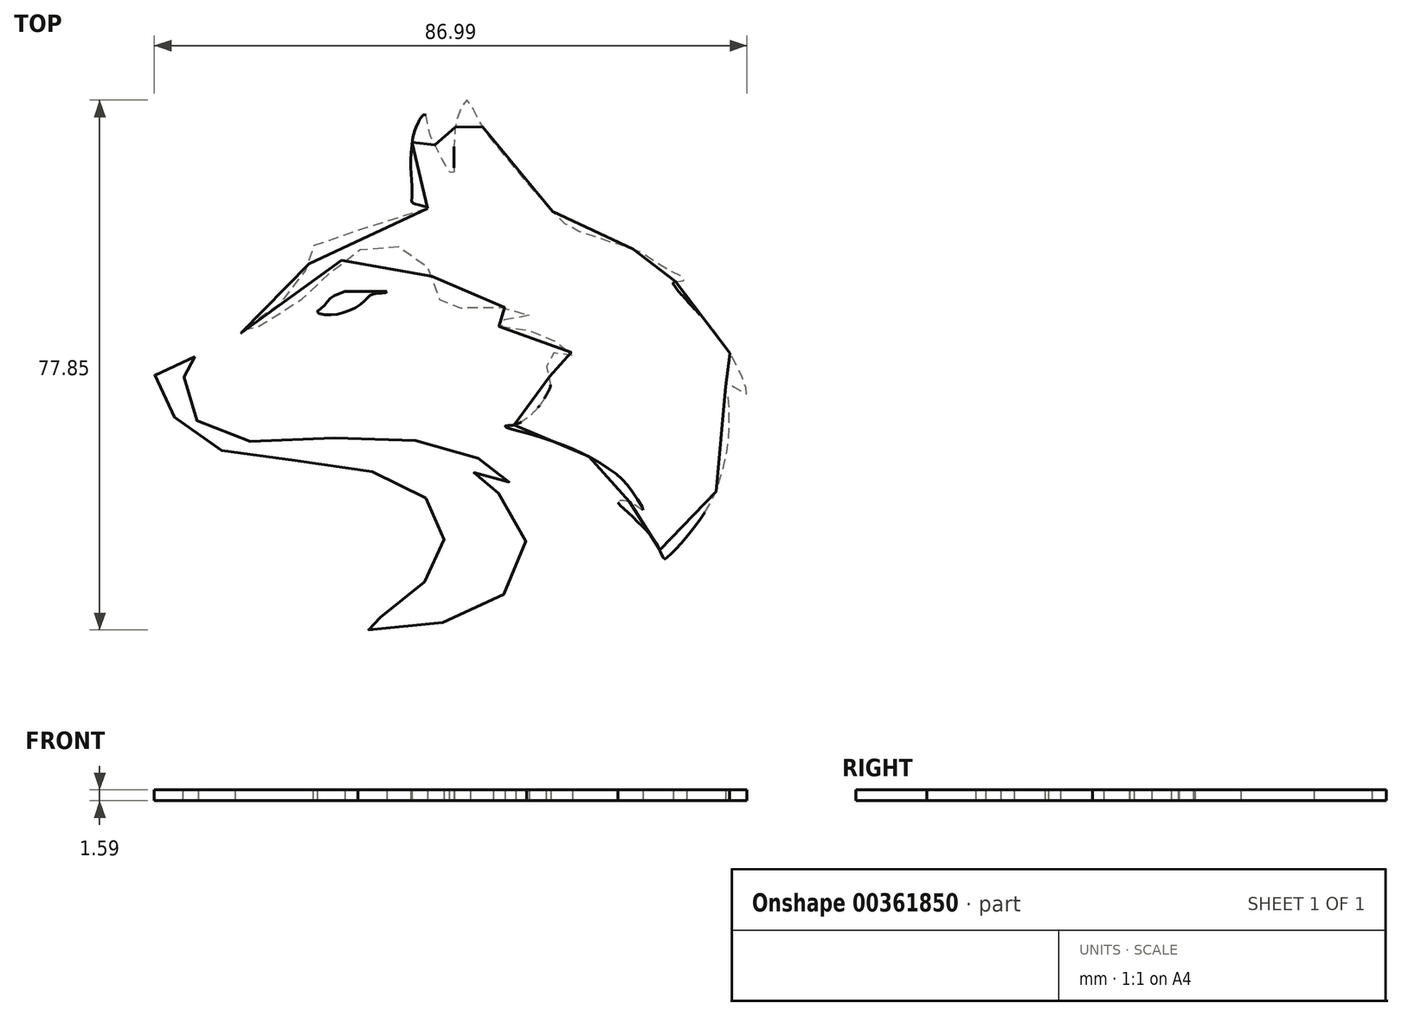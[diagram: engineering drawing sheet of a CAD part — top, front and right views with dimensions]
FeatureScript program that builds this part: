
annotation { "Feature Type Name" : "Feature", "Feature Type Description" : "" }
export const myFeature = defineFeature(function(context is Context, id is Id, definition is map)
    precondition{}
    {
        {
            var Q0;
            Q0=qCreatedBy(makeId("Top.planeOp"),FACE);
            var sketch = newSketch(context, id + "F0", { "sketchPlane" : qUnion([Q0])});
            skLineSegment(sketch, "E0", {"start": v(-16.32, 7.14) * mm, "end": v(-22.48, 7.14) * mm});
            skFitSpline(sketch, "E1", {"points": [v(-22.48, 7.14) * mm, v(-24.21, 6.43) * mm, v(-25.02, 5.67) * mm, v(-25.89, 4.75) * mm, v(-26.55, 4.09) * mm, v(-25.23, 3.68) * mm, v(-23.1, 3.94) * mm, v(-20.85, 4.8) * mm, v(-19.48, 5.87) * mm, v(-18.87, 6.48) * mm, v(-18.18, 6.79) * mm, v(-17.18, 6.91) * mm, v(-16.62, 6.93) * mm, v(-16.32, 7.14) * mm], "startDerivative": vector(-19.93, -6.66) * mm, "endDerivative": vector(6.3, 6.23) * mm});
            skFitSpline(sketch, "E2", {"points": [v(-44.5, -2.46) * mm, v(-47.41, -2.83) * mm, v(-49.23, -3.92) * mm, v(-50.43, -5.36) * mm, v(-49.87, -7.6) * mm, v(-48.8, -9.55) * mm, v(-46.81, -12.25) * mm, v(-44.76, -14.33) * mm, v(-40.01, -16.38) * mm, v(-33.9, -17.35) * mm, v(-27.74, -17.9) * mm, v(-20.44, -18.9) * mm, v(-15.66, -20.2) * mm, v(-11.9, -22.07) * mm, v(-9.77, -24.2) * mm, v(-8.51, -26.32) * mm, v(-7.97, -28.58) * mm, v(-8.15, -30.96) * mm, v(-9.37, -33.55) * mm, v(-10.56, -35.31) * mm, v(-13.6, -38.29) * mm, v(-16.28, -40.2) * mm, v(-18.26, -41.32) * mm, v(-19.45, -41.9) * mm, v(-20.56, -42.5) * mm, v(-19.4, -42.58) * mm, v(-13.55, -42.18) * mm, v(-7.21, -41.32) * mm, v(-1.82, -39.37) * mm, v(1.5, -36.71) * mm, v(3.94, -32.76) * mm, v(4.08, -29.52) * mm, v(2.86, -25.92) * mm, v(0.7, -23.11) * mm, v(-1.31, -21.39) * mm, v(-3.62, -19.95) * mm, v(-4.07, -19.8) * mm, v(-3.92, -19.66) * mm, v(-3.03, -19.36) * mm, v(-1.44, -19.53) * mm, v(0.03, -20.09) * mm, v(1.43, -20.74) * mm, v(2.54, -21.3) * mm, v(2.56, -21.05) * mm, v(-1.4, -18.21) * mm, v(-6.33, -16) * mm, v(-10.93, -14.95) * mm, v(-15.83, -14.52) * mm, v(-24.9, -14.4) * mm, v(-33.11, -14.73) * mm, v(-39.25, -14.68) * mm, v(-42.45, -13.26) * mm, v(-44.76, -11.21) * mm, v(-46, -8.6) * mm, v(-46.3, -6.42) * mm, v(-45.57, -4.37) * mm, v(-44.45, -3.25) * mm, v(-44.18, -2.93) * mm, v(-44, -2.64) * mm, v(-44.02, -2.47) * mm, v(-44.5, -2.46) * mm]});
            skFitSpline(sketch, "E3", {"points": [v(-10.37, 19.36) * mm, v(-22.35, 15.68) * mm, v(-27.15, 13.71) * mm, v(-27.15, 13.03) * mm, v(-28.26, 10.29) * mm, v(-31.6, 5.75) * mm, v(-35.36, 2.67) * mm, v(-38.61, 0.88) * mm, v(-34.93, 2.08) * mm, v(-28.77, 6.01) * mm, v(-25.43, 8.92) * mm, v(-23.04, 11.66) * mm, v(-19.19, 13.63) * mm, v(-15, 13.8) * mm, v(-11.66, 12.43) * mm, v(-9.6, 9.18) * mm, v(-8.58, 6.1) * mm, v(-8.4, 4.9) * mm, v(-6.27, 4.73) * mm, v(-1.4, 4.81) * mm, v(2.37, 4.64) * mm, v(4.6, 3.79) * mm, v(3.91, 3.27) * mm, v(1.86, 3.02) * mm, v(-0.2, 2.67) * mm, v(-0.7, 2.16) * mm, v(0.32, 1.99) * mm, v(2.55, 1.73) * mm, v(4.81, 1.35) * mm, v(7.25, 0.4) * mm, v(8.96, -0.53) * mm, v(10.37, -1.6) * mm, v(10.93, -2.07) * mm, v(10.59, -2.46) * mm, v(9.56, -2.37) * mm, v(8.54, -2.03) * mm, v(7.47, -1.78) * mm, v(7.08, -2.5) * mm, v(7.12, -4) * mm, v(7.45, -5.02) * mm, v(7.66, -5.7) * mm, v(7.66, -6.85) * mm, v(7.2, -7.86) * mm, v(6.37, -9.26) * mm, v(4.86, -10.96) * mm, v(3.67, -11.86) * mm, v(2.48, -12.43) * mm, v(1.51, -12.57) * mm, v(1.04, -12.61) * mm, v(1.09, -12.75) * mm, v(2.62, -13.27) * mm, v(8.84, -15.14) * mm, v(13.74, -17.35) * mm, v(17.73, -20.02) * mm, v(19.85, -22.5) * mm, v(21.3, -24.98) * mm, v(20.82, -24.74) * mm, v(19.06, -23.7) * mm, v(17.73, -23.65) * mm, v(17.61, -23.89) * mm, v(18.7, -24.98) * mm, v(20.88, -27.1) * mm, v(22.71, -29.07) * mm, v(23.78, -30.95) * mm, v(24.4, -32.17) * mm, v(24.7, -32.07) * mm, v(26.63, -30.14) * mm, v(29.53, -26.52) * mm, v(31.97, -22.25) * mm, v(33.5, -16.86) * mm, v(33.85, -14.06) * mm, v(33.81, -8.54) * mm, v(33.4, -7.01) * mm, v(33.46, -6.35) * mm, v(33.71, -6.2) * mm, v(34.58, -6.86) * mm, v(36.15, -7.78) * mm, v(36.5, -7.88) * mm, v(35.95, -5.8) * mm, v(34.37, -2.54) * mm, v(31.98, 0.97) * mm, v(28.73, 4.69) * mm, v(26.49, 7.18) * mm, v(25.72, 8.25) * mm, v(25.72, 8.45) * mm, v(26.18, 8.6) * mm, v(27.25, 8.76) * mm, v(27.7, 8.91) * mm, v(26.7, 9.47) * mm, v(24.22, 10.69) * mm, v(22.04, 12.26) * mm, v(19.74, 13.41) * mm, v(17.2, 14.2) * mm, v(14.24, 15.16) * mm, v(11.45, 16.13) * mm, v(9.46, 17.4) * mm, v(7.04, 20) * mm, v(4.07, 23.33) * mm, v(0.86, 27.27) * mm, v(-1.56, 30.23) * mm, v(-2.95, 32.53) * mm, v(-3.98, 34.59) * mm, v(-4.28, 35.12) * mm, v(-4.53, 35.25) * mm, v(-4.78, 35.1) * mm, v(-5.38, 34.35) * mm, v(-5.84, 33.09) * mm, v(-6.24, 31.58) * mm, v(-6.44, 29.5) * mm, v(-6.44, 24.7) * mm, v(-6.45, 24.65) * mm, v(-7.15, 24.67) * mm, v(-7.16, 24.74) * mm, v(-7.74, 25.72) * mm, v(-8.92, 27.99) * mm, v(-9.82, 29.8) * mm, v(-10.3, 31.59) * mm, v(-10.49, 32.8) * mm, v(-10.66, 33.1) * mm, v(-11.08, 33.03) * mm, v(-11.62, 32.14) * mm, v(-12.14, 31.13) * mm, v(-12.8, 27.09) * mm, v(-12.67, 23.34) * mm, v(-12.67, 20.87) * mm, v(-12.6, 20.2) * mm, v(-11.73, 19.87) * mm, v(-10.83, 19.66) * mm, v(-10.37, 19.36) * mm]});
            skSolve(sketch);
        }
        {
            var Q0;
            Q0=makeQuery(id+"F0.imprint","IMPRINT",FACE,{"disambiguationData":[TD([[makeQuery(id+"F0.imprint","IMPRINT",EDGE,{"derivedFrom":sQuery(id+"F0.wireOp",EDGE,"E3")}),1.0]])]});
            var Q1;
            Q1=makeQuery(id+"F0.imprint","IMPRINT",FACE,{"disambiguationData":[TD([[makeQuery(id+"F0.imprint","IMPRINT",EDGE,{"derivedFrom":sQuery(id+"F0.wireOp",EDGE,"E2")}),1.0]])]});
            var Q2;
            Q2=makeQuery(id+"F0.imprint","IMPRINT",FACE,{"disambiguationData":[TD([[makeQuery(id+"F0.imprint","IMPRINT",EDGE,{"derivedFrom":sQuery(id+"F0.wireOp",EDGE,"E0")}),1.0]])]});
            extrude(context, id + "F1", {"entities" : qUnion([Q0, Q1, Q2]), "depth" : 1.59 * mm});
        }
    });
